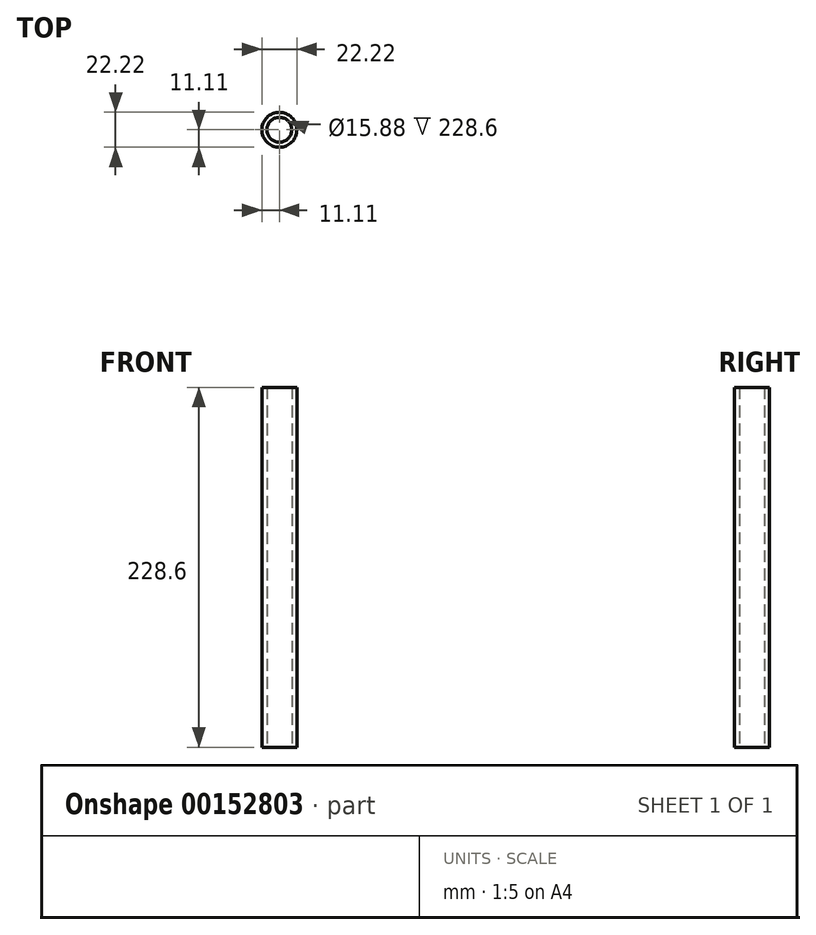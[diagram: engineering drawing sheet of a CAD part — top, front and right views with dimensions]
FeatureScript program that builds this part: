
annotation { "Feature Type Name" : "Feature", "Feature Type Description" : "" }
export const myFeature = defineFeature(function(context is Context, id is Id, definition is map)
    precondition{}
    {
        {
            var Q0;
            Q0=qCreatedBy(makeId("Top.planeOp"),FACE);
            var sketch = newSketch(context, id + "F0", { "sketchPlane" : qUnion([Q0])});
            skCircle(sketch, "E0", {"center": v(0, 0) * mm, "radius": 11.11 * mm});
            skCircle(sketch, "E1", {"center": v(0, 0) * mm, "radius": 7.94 * mm});
            skSolve(sketch);
        }
        {
            var Q0;
            Q0=qSketchRegion(id+"F0",true);
            extrude(context, id + "F1", {"entities" : qUnion([Q0]), "depth" : 228.6 * mm});
        }
    });
